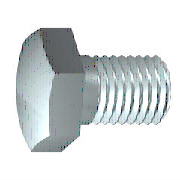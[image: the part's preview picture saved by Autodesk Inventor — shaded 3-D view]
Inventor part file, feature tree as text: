
AUTODESK INVENTOR PART (.ipt)
format: ipt  version: 2013 (Build 170138000, 138)  size: 186,368 bytes
history: native  units: mm (DEFAULTED — no unit token found)
features: sketch x2, extrude x1, chamfer x1, plane x1
ambient origin geometry x7: Origin, YZ Plane, XZ Plane, X Axis, Y Axis, Z Axis, Center Point
bodies: Solid1 (feature_tree), Body (feature_tree)
feature tree (5):
  extrude  "Head"  TaperAngle=90.0deg  [1 undecoded]
  chamfer  "Chamfer1"  [1 undecoded]
  plane  "Work Plane1"
  sketch  "Sketch1"  dims[d2=8.0mm d12=90.0deg]
  sketch  "Sketch2"  dims[d3=5.68mm d4=0.0mm d21=90.0deg d6=0.766813mm d7=0.766912mm d8=0.0mm d11=13.0mm d15=22.0mm d16=0.0mm d55=45.0deg d58=0.0mm d59=35.0mm d65=13.0mm d67=30.0deg d68=15.6mm d69=5.68mm d71=0.1mm d73=0.0mm]
note: 2 required parameter values undecoded (feature->parameter linkage not recoverable at this tier; creation-order binding heuristic only, values carry confidence <= 0.55)
